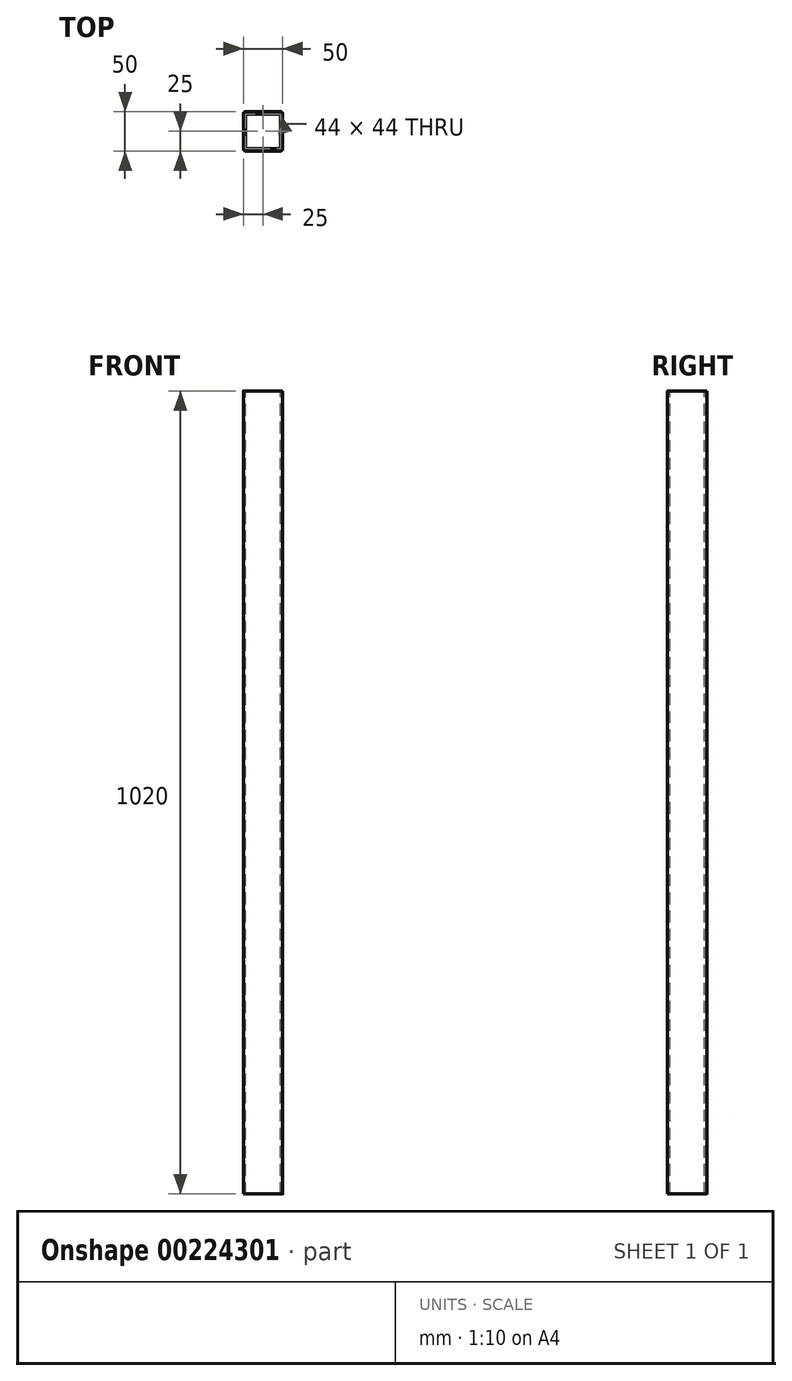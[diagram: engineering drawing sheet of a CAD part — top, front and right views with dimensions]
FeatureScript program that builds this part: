
annotation { "Feature Type Name" : "Feature", "Feature Type Description" : "" }
export const myFeature = defineFeature(function(context is Context, id is Id, definition is map)
    precondition{}
    {
        {
            var Q0;
            Q0=qCreatedBy(makeId("Top.planeOp"),FACE);
            var sketch = newSketch(context, id + "F0", { "sketchPlane" : qUnion([Q0])});
            skLineSegment(sketch, "E0.bottom", {"start": v(22, 25) * mm, "end": v(-22, 25) * mm});
            skLineSegment(sketch, "E0.top", {"start": v(22, -25) * mm, "end": v(-22, -25) * mm});
            skLineSegment(sketch, "E0.left", {"start": v(25, 22) * mm, "end": v(25, -22) * mm});
            skLineSegment(sketch, "E0.right", {"start": v(-25, 22) * mm, "end": v(-25, -22) * mm});
            skPoint(sketch, "E0.middle", {"position": v(0, 0) * mm});
            skPoint(sketch, "E1.visualSharp", {"position": v(-25, 25) * mm});
            skArc(sketch, "E1.filletArc", {"start": v(-22, 25) * mm, "mid": v(-24.12, 24.12) * mm, "end": v(-25, 22) * mm});
            skPoint(sketch, "E2.visualSharp", {"position": v(25, 25) * mm});
            skArc(sketch, "E2.filletArc", {"start": v(25, 22) * mm, "mid": v(24.12, 24.12) * mm, "end": v(22, 25) * mm});
            skPoint(sketch, "E3.visualSharp", {"position": v(25, -25) * mm});
            skArc(sketch, "E3.filletArc", {"start": v(22, -25) * mm, "mid": v(24.12, -24.12) * mm, "end": v(25, -22) * mm});
            skPoint(sketch, "E4.visualSharp", {"position": v(-25, -25) * mm});
            skArc(sketch, "E4.filletArc", {"start": v(-25, -22) * mm, "mid": v(-24.12, -24.12) * mm, "end": v(-22, -25) * mm});
            skLineSegment(sketch, "E5.0", {"start": v(-22, 22) * mm, "end": v(-22, -22) * mm});
            skLineSegment(sketch, "E5.1", {"start": v(22, 22) * mm, "end": v(-22, 22) * mm});
            skLineSegment(sketch, "E5.2", {"start": v(22, 22) * mm, "end": v(22, -22) * mm});
            skLineSegment(sketch, "E5.3", {"start": v(22, -22) * mm, "end": v(-22, -22) * mm});
            skSolve(sketch);
        }
        {
            var Q0;
            Q0=makeQuery(id+"F0.imprint","IMPRINT",FACE,{"disambiguationData":[TD([[makeQuery(id+"F0.imprint","IMPRINT",EDGE,{"derivedFrom":sQuery(id+"F0.wireOp",EDGE,"E0.bottom")}),1.0]])]});
            extrude(context, id + "F1", {"entities" : qUnion([Q0]), "oppositeDirection" : true, "depth" : 1020 * mm});
        }
    });
